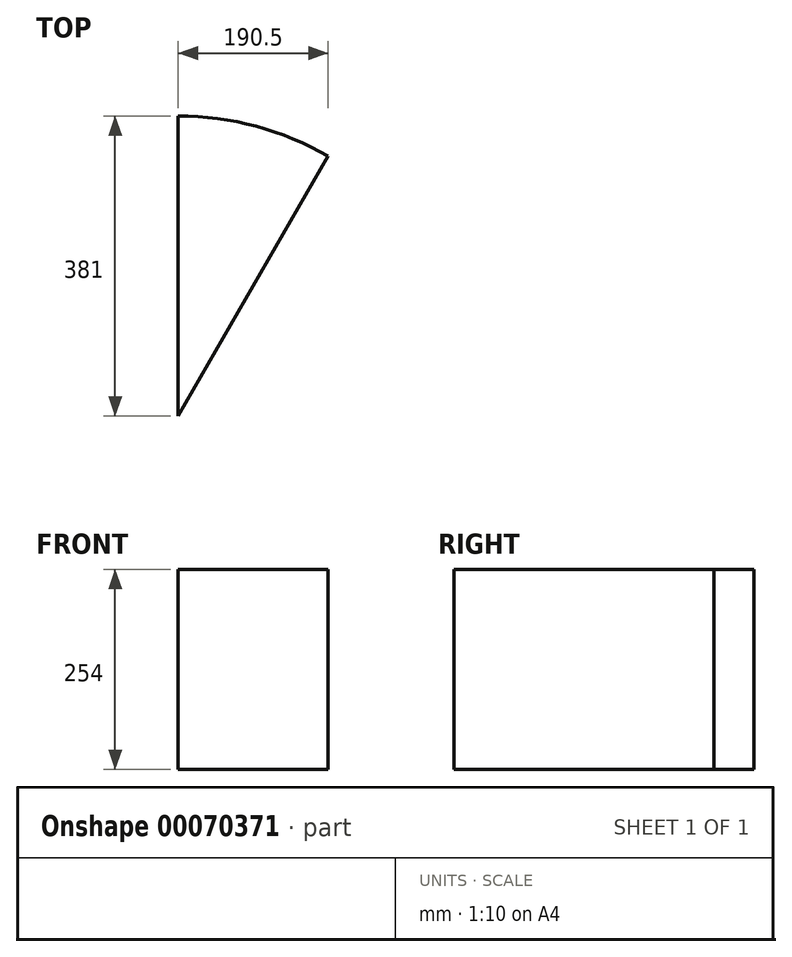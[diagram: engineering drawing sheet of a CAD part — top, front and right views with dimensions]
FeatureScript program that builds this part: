
annotation { "Feature Type Name" : "Feature", "Feature Type Description" : "" }
export const myFeature = defineFeature(function(context is Context, id is Id, definition is map)
    precondition{}
    {
        {
            var Q0;
            Q0=qCreatedBy(makeId("Right.planeOp"),FACE);
            var sketch = newSketch(context, id + "F0", { "sketchPlane" : qUnion([Q0])});
            skLineSegment(sketch, "E0.bottom", {"start": v(-297.46, 0) * mm, "end": v(83.54, 0) * mm});
            skLineSegment(sketch, "E0.top", {"start": v(-297.46, 254) * mm, "end": v(83.54, 254) * mm});
            skLineSegment(sketch, "E0.left", {"start": v(-297.46, 0) * mm, "end": v(-297.46, 254) * mm});
            skLineSegment(sketch, "E0.right", {"start": v(83.54, 0) * mm, "end": v(83.54, 254) * mm});
            skSolve(sketch);
        }
        {
            var Q0;
            Q0=makeQuery(id+"F0.imprint","IMPRINT",FACE,{"disambiguationData":[TD([[makeQuery(id+"F0.imprint","IMPRINT",EDGE,{"derivedFrom":sQuery(id+"F0.wireOp",EDGE,"E0.bottom")}),1.0]])]});
            var Q1;
            Q1=sQuery(id+"F0.wireOp",EDGE,"E0.left");
            revolve(context, id + "F1", {"entities" : qUnion([Q0]), "axis" : qUnion([Q1]), "revolveType" : RevolveType.ONE_DIRECTION, "oppositeDirection" : true, "angle" : 30 * degree});
        }
    });
